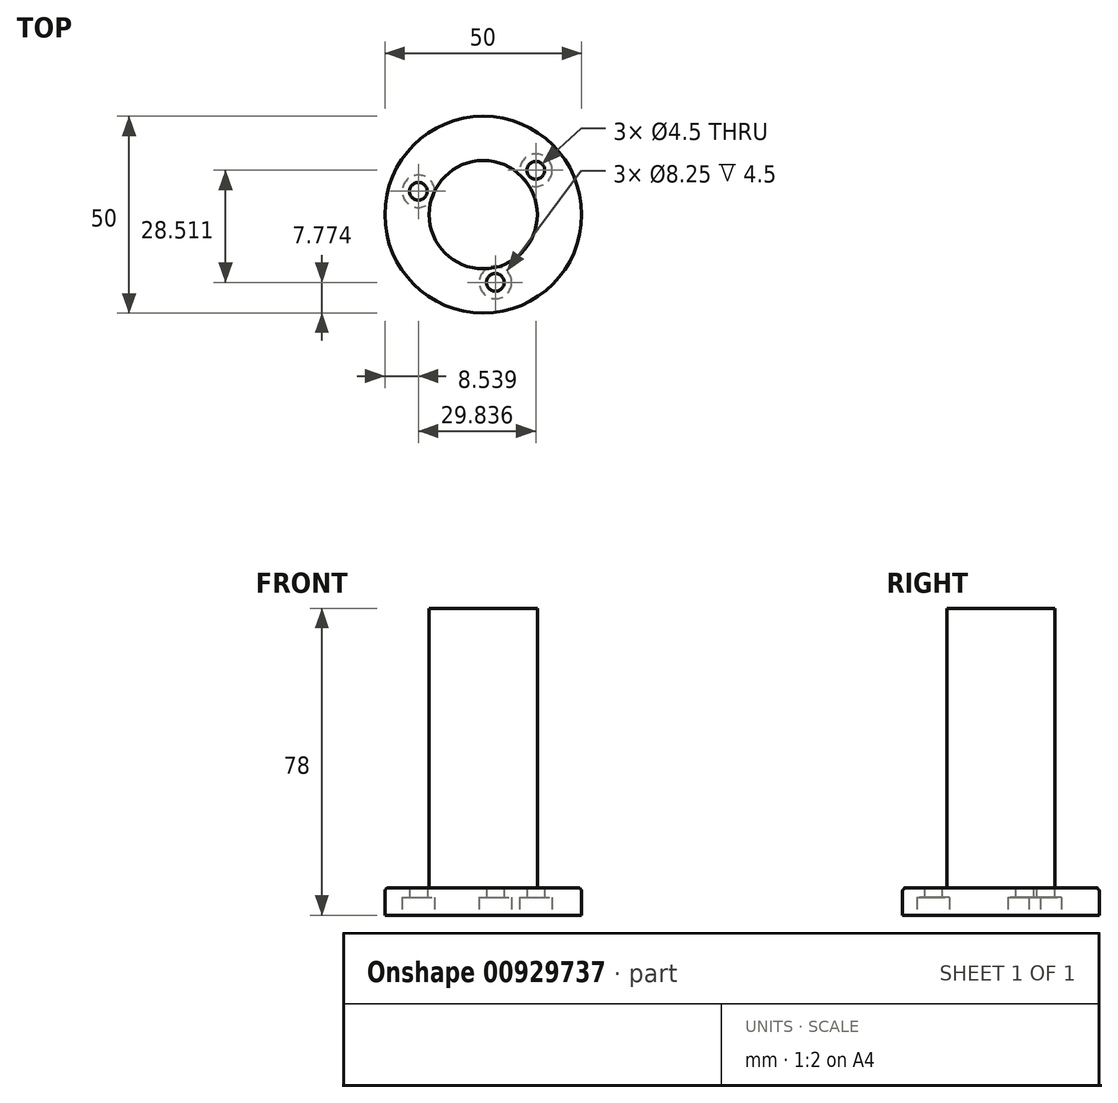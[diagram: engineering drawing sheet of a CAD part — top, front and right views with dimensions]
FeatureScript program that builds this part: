
annotation { "Feature Type Name" : "Feature", "Feature Type Description" : "" }
export const myFeature = defineFeature(function(context is Context, id is Id, definition is map)
    precondition{}
    {
        {
            var Q0;
            Q0=qCreatedBy(makeId("Top.planeOp"),FACE);
            var sketch = newSketch(context, id + "F0", { "sketchPlane" : qUnion([Q0])});
            skCircle(sketch, "E0", {"center": v(0, 0) * mm, "radius": 25 * mm});
            skCircle(sketch, "E1", {"center": v(0, 0) * mm, "radius": 13.75 * mm});
            skCircle(sketch, "E2", {"center": v(0, 0) * mm, "radius": 17.5 * mm, "construction": true});
            skPoint(sketch, "E3", {"position": v(13.38, 11.28) * mm});
            skPoint(sketch, "E4.1.0", {"position": v(-16.46, 5.94) * mm});
            skPoint(sketch, "E4.2.0", {"position": v(3.09, -17.23) * mm});
            skSolve(sketch);
        }
        {
            var Q0;
            Q0 = qSketchRegion(id + "F0", true);
            extrude(context, id + "F1", {"entities" : qUnion([Q0]), "depth" : 7 * mm, "offsetDistance" : 25 * mm});
        }
        {
            var Q0;
            Q0=makeQuery(id+"F0.imprint","IMPRINT",FACE,{"disambiguationData":[TD([[makeQuery(id+"F0.imprint","IMPRINT",EDGE,{"derivedFrom":sQuery(id+"F0.wireOp",EDGE,"E1")}),1.0]])]});
            extrude(context, id + "F2", {"entities" : qUnion([Q0]), "operationType" : NewBodyOperationType.ADD, "depth" : 78 * mm, "offsetDistance" : 25 * mm});
        }
        {
            var Q0;
            Q0=sQuery(id+"F0.wireOp",VERTEX,"E4.2.0");
            var Q1;
            Q1=sQuery(id+"F0.wireOp",VERTEX,"E3");
            var Q2;
            Q2=sQuery(id+"F0.wireOp",VERTEX,"E4.1.0");
            var Q3;
            Q3=makeQuery(id+"F1.opExtrude","SWEPT_BODY",BODY,{"disambiguationData":[OSD([sQuery(id+"F0.wireOp",EDGE,"E0"),sQuery(id+"F0.wireOp",EDGE,"E1")])]});
            hole(context, id + "F3", {"style" : HoleStyle.C_BORE, "endStyle" : HoleEndStyle.THROUGH, "oppositeDirection" : true, "holeDiameter" : 4.5 * mm, "cBoreDiameter" : 8.25 * mm, "cBoreDepth" : 4.5 * mm, "majorDiameter" : 5 * mm, "isTappedThrough" : true, "tappedDepth" : 12 * mm, "tapClearance" : 3, "startFromSketch" : true, "locations" : qUnion([Q0, Q1, Q2]), "scope" : qUnion([Q3])});
        }
        {
            var Q0;
            Q0=makeQuery(id+"F1.opExtrude","CAP_EDGE",EDGE,{"disambiguationData":[OSD([sQuery(id+"F0.wireOp",EDGE,"E0")])],"isStart":false});
            fillet(context, id + "F4", {"entities" : qUnion([Q0]), "radius" : 1 * mm, "tangentPropagation" : true, "allowEdgeOverflow" : false});
        }
    });
